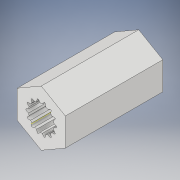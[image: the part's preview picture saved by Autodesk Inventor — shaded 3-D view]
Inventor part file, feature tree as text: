
AUTODESK INVENTOR PART (.ipt)
format: ipt  version: 2019 (Build 230136000, 136)  size: 561,152 bytes
history: native  units: in
note: dims shown in document units (in); Inventor stores cm internally (conversion verified against a paired STEP export)
features: extrude x3, sketch x3, projected_geometry x1, other x1
ambient origin geometry x8: Origin, YZ Plane, XZ Plane, XY Plane, X Axis, Y Axis, Z Axis, Center Point
bodies: Solid1 (feature_tree)
feature tree (8):
  extrude  "Extrusion1"  TaperAngle=0.0deg  [1 undecoded]
  extrude  "Extrusion2"  Depth=0.9916in TaperAngle=0.0deg
  extrude  "Extrusion3"  [1 undecoded]
  sketch  "Sketch1"  dims[d1=0.49in d2=0.0in d3=0.0in]
  sketch  "Sketch2"  dims[d4=0.0in d5=0.0in d6=0.9916in d7=0.0in]
  sketch  "Sketch3"
  projected_geometry  "Projected Loop1"
  other  "Boss-Extrude2"
note: 2 required parameter values undecoded (feature->parameter linkage not recoverable at this tier; creation-order binding heuristic only, values carry confidence <= 0.55)
